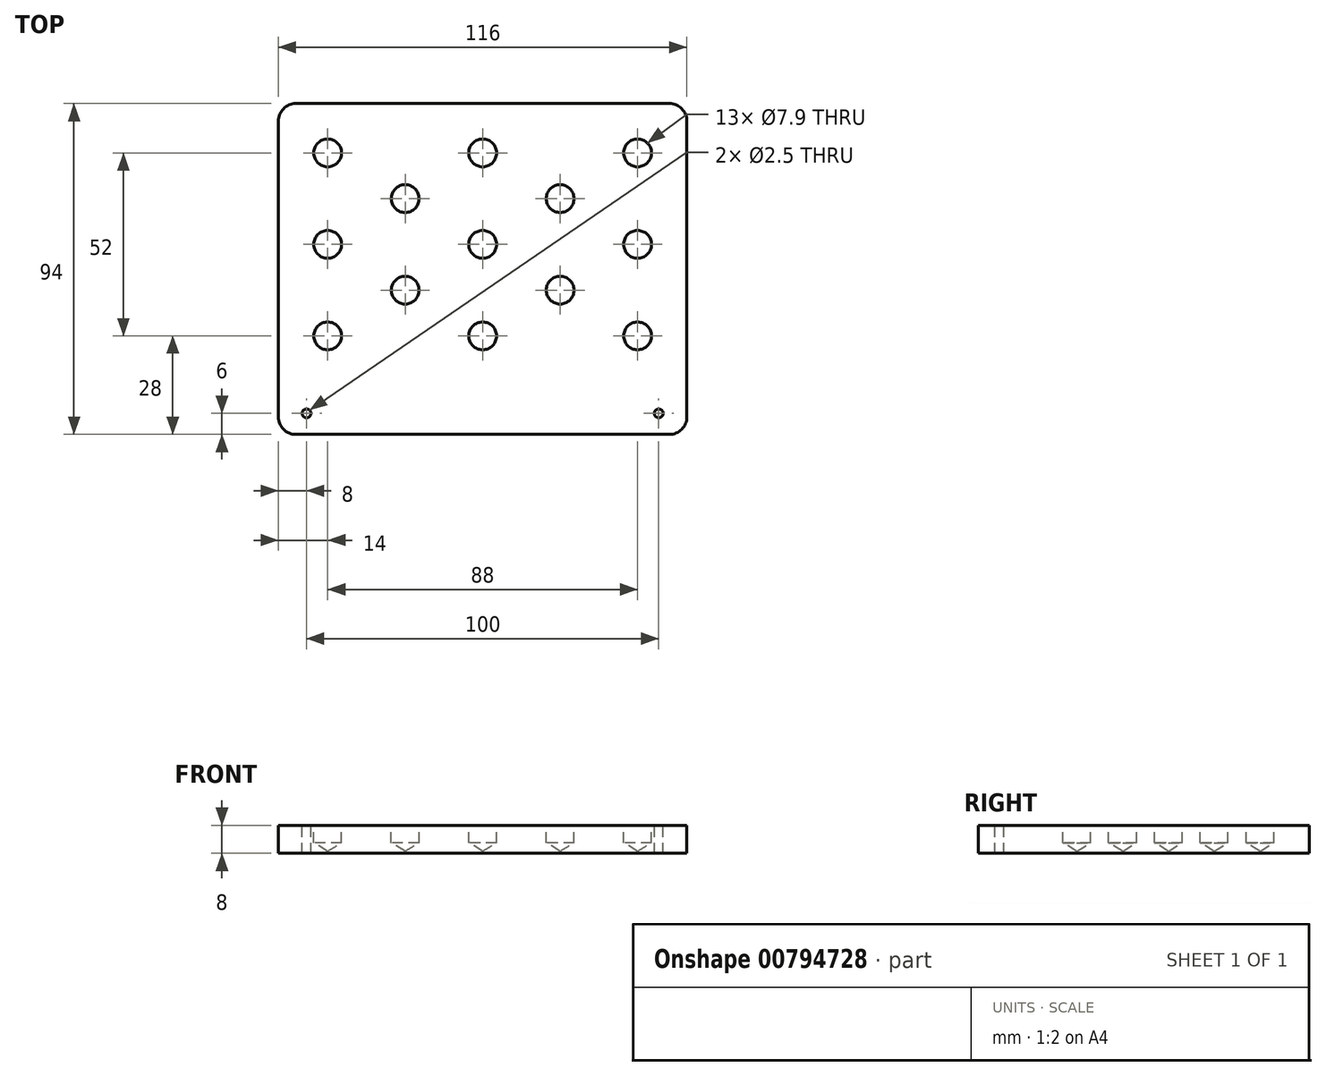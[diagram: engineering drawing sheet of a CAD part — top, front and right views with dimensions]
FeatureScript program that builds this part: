
annotation { "Feature Type Name" : "Feature", "Feature Type Description" : "" }
export const myFeature = defineFeature(function(context is Context, id is Id, definition is map)
    precondition{}
    {
        {
            var Q0;
            Q0=qCreatedBy(makeId("Top.planeOp"),FACE);
            var sketch = newSketch(context, id + "F0", { "sketchPlane" : qUnion([Q0])});
            skLineSegment(sketch, "E0.bottom", {"start": v(-58, 47) * mm, "end": v(58, 47) * mm});
            skLineSegment(sketch, "E0.top", {"start": v(-58, -47) * mm, "end": v(58, -47) * mm});
            skLineSegment(sketch, "E0.left", {"start": v(-58, 47) * mm, "end": v(-58, -47) * mm});
            skLineSegment(sketch, "E0.right", {"start": v(58, 47) * mm, "end": v(58, -47) * mm});
            skPoint(sketch, "E0.middle", {"position": v(0, 0) * mm});
            skSolve(sketch);
        }
        {
            var Q0;
            Q0=makeQuery(id+"F0.imprint","IMPRINT",FACE,{"disambiguationData":[TD([[makeQuery(id+"F0.imprint","IMPRINT",EDGE,{"derivedFrom":sQuery(id+"F0.wireOp",EDGE,"E0.bottom")}),-1.0]])]});
            extrude(context, id + "F1", {"entities" : qUnion([Q0]), "depth" : 8 * mm, "offsetDistance" : 25 * mm});
        }
        {
            var Q0;
            Q0=makeQuery(id+"F1.opExtrude","CAP_FACE",FACE,{"disambiguationData":[OSD([sQuery(id+"F0.wireOp",EDGE,"E0.bottom"),sQuery(id+"F0.wireOp",EDGE,"E0.top"),sQuery(id+"F0.wireOp",EDGE,"E0.left"),sQuery(id+"F0.wireOp",EDGE,"E0.right")])],"isStart":false});
            var sketch = newSketch(context, id + "F2", { "sketchPlane" : qUnion([Q0])});
            skLineSegment(sketch, "E1", {"start": v(-58, -32) * mm, "end": v(58, -32) * mm, "construction": true});
            skLineSegment(sketch, "E2", {"start": v(-58, -19) * mm, "end": v(58, -19) * mm, "construction": true});
            skLineSegment(sketch, "E3", {"start": v(58, -19) * mm, "end": v(58, -6) * mm, "construction": true});
            skLineSegment(sketch, "E4", {"start": v(58, -6) * mm, "end": v(-58, -6) * mm, "construction": true});
            skLineSegment(sketch, "E5", {"start": v(-58, -6) * mm, "end": v(-58, 7) * mm, "construction": true});
            skLineSegment(sketch, "E6", {"start": v(-58, 7) * mm, "end": v(58, 7) * mm, "construction": true});
            skLineSegment(sketch, "E7", {"start": v(58, 7) * mm, "end": v(58, 20) * mm, "construction": true});
            skLineSegment(sketch, "E8", {"start": v(58, 20) * mm, "end": v(-58, 20) * mm, "construction": true});
            skLineSegment(sketch, "E9.bottom", {"start": v(-58, -37) * mm, "end": v(58, -37) * mm, "construction": true});
            skLineSegment(sketch, "E9.top", {"start": v(-58, -45) * mm, "end": v(58, -45) * mm, "construction": true});
            skLineSegment(sketch, "E9.left", {"start": v(-58, -37) * mm, "end": v(-58, -45) * mm, "construction": true});
            skLineSegment(sketch, "E9.right", {"start": v(58, -37) * mm, "end": v(58, -45) * mm, "construction": true});
            skLineSegment(sketch, "E10", {"start": v(-44, 47) * mm, "end": v(-44, -32) * mm, "construction": true});
            skLineSegment(sketch, "E11", {"start": v(-44, -32) * mm, "end": v(-22, -32) * mm, "construction": true});
            skLineSegment(sketch, "E12", {"start": v(-22, -32) * mm, "end": v(-22, 47) * mm, "construction": true});
            skLineSegment(sketch, "E13", {"start": v(-22, 47) * mm, "end": v(0, 47) * mm, "construction": true});
            skLineSegment(sketch, "E14", {"start": v(0, 47) * mm, "end": v(0, -32) * mm, "construction": true});
            skLineSegment(sketch, "E15", {"start": v(0, -32) * mm, "end": v(22, -32) * mm, "construction": true});
            skLineSegment(sketch, "E16", {"start": v(22, -32) * mm, "end": v(22, 47) * mm, "construction": true});
            skLineSegment(sketch, "E17", {"start": v(22, 47) * mm, "end": v(44, 47) * mm, "construction": true});
            skLineSegment(sketch, "E18", {"start": v(44, 47) * mm, "end": v(44, -32) * mm, "construction": true});
            skLineSegment(sketch, "E19", {"start": v(44, -32) * mm, "end": v(44.94, -32) * mm, "construction": true});
            skPoint(sketch, "E20", {"position": v(-44, 7) * mm});
            skPoint(sketch, "E21", {"position": v(-44, -6) * mm});
            skPoint(sketch, "E22", {"position": v(-22, -19) * mm});
            skPoint(sketch, "E23", {"position": v(-22, 20) * mm});
            skPoint(sketch, "E24", {"position": v(0, 7) * mm});
            skPoint(sketch, "E25", {"position": v(0, -6) * mm});
            skPoint(sketch, "E26", {"position": v(22, -19) * mm});
            skPoint(sketch, "E27", {"position": v(22, 7) * mm});
            skCircle(sketch, "E28", {"center": v(-44, 7) * mm, "radius": 12 * mm});
            skCircle(sketch, "E29", {"center": v(-22, 20) * mm, "radius": 12 * mm});
            skPoint(sketch, "E30", {"position": v(-22, -6) * mm});
            skCircle(sketch, "E31", {"center": v(-22, -6) * mm, "radius": 12 * mm});
            skCircle(sketch, "E32", {"center": v(0, 7) * mm, "radius": 12 * mm});
            skPoint(sketch, "E33", {"position": v(-44, -19) * mm});
            skPoint(sketch, "E34", {"position": v(0, -19) * mm});
            skPoint(sketch, "E35", {"position": v(22, 20) * mm});
            skPoint(sketch, "E36", {"position": v(22, -6) * mm});
            skCircle(sketch, "E37", {"center": v(-44, -19) * mm, "radius": 12 * mm});
            skCircle(sketch, "E38", {"center": v(0, -19) * mm, "radius": 12 * mm});
            skCircle(sketch, "E39", {"center": v(22, -6) * mm, "radius": 12 * mm});
            skCircle(sketch, "E40", {"center": v(22, 20) * mm, "radius": 12 * mm});
            skPoint(sketch, "E41", {"position": v(44, 7) * mm});
            skPoint(sketch, "E42", {"position": v(44, -19) * mm});
            skCircle(sketch, "E43", {"center": v(44, 7) * mm, "radius": 12 * mm});
            skCircle(sketch, "E44", {"center": v(44, -19) * mm, "radius": 12 * mm});
            skLineSegment(sketch, "E45", {"start": v(-58, 33) * mm, "end": v(58, 33) * mm, "construction": true});
            skPoint(sketch, "E46", {"position": v(-44, 33) * mm});
            skPoint(sketch, "E47", {"position": v(0, 33) * mm});
            skPoint(sketch, "E48", {"position": v(44, 33) * mm});
            skCircle(sketch, "E49", {"center": v(-44, 33) * mm, "radius": 12 * mm});
            skCircle(sketch, "E50", {"center": v(0, 33) * mm, "radius": 12 * mm});
            skCircle(sketch, "E51", {"center": v(44, 33) * mm, "radius": 12 * mm});
            skSolve(sketch);
        }
        {
            var Q0;
            Q0=sQuery(id+"F2.wireOp",VERTEX,"E46");
            var Q1;
            Q1=sQuery(id+"F2.wireOp",VERTEX,"E23");
            var Q2;
            Q2=sQuery(id+"F2.wireOp",VERTEX,"E20");
            var Q3;
            Q3=sQuery(id+"F2.wireOp",VERTEX,"E33");
            var Q4;
            Q4=sQuery(id+"F2.wireOp",VERTEX,"E30");
            var Q5;
            Q5=sQuery(id+"F2.wireOp",VERTEX,"E34");
            var Q6;
            Q6=sQuery(id+"F2.wireOp",VERTEX,"E24");
            var Q7;
            Q7=sQuery(id+"F2.wireOp",VERTEX,"E47");
            var Q8;
            Q8=sQuery(id+"F2.wireOp",VERTEX,"E35");
            var Q9;
            Q9=sQuery(id+"F2.wireOp",VERTEX,"E36");
            var Q10;
            Q10=sQuery(id+"F2.wireOp",VERTEX,"E41");
            var Q11;
            Q11=sQuery(id+"F2.wireOp",VERTEX,"E48");
            var Q12;
            Q12=sQuery(id+"F2.wireOp",VERTEX,"E42");
            var Q13;
            Q13=makeQuery(id+"F1.opExtrude","SWEPT_BODY",BODY,{"disambiguationData":[OSD([sQuery(id+"F0.wireOp",EDGE,"E0.bottom"),sQuery(id+"F0.wireOp",EDGE,"E0.top"),sQuery(id+"F0.wireOp",EDGE,"E0.left"),sQuery(id+"F0.wireOp",EDGE,"E0.right")])]});
            hole(context, id + "F3", {"style" : HoleStyle.SIMPLE, "endStyle" : HoleEndStyle.BLIND, "standardTappedOrClearance" : lookupTablePath({ "standard" : "ISO", "size" : "7.9", "type" : "Drilled" }), "standardBlindInLast" : lookupTablePath({ "standard" : "ISO", "size" : "7.9", "type" : "Drilled" }), "holeDiameter" : 7.9 * mm, "majorDiameter" : 5 * mm, "holeDepth" : 5 * mm, "isTappedThrough" : true, "tappedDepth" : 12 * mm, "tapClearance" : 3, "locations" : qUnion([Q0, Q1, Q2, Q3, Q4, Q5, Q6, Q7, Q8, Q9, Q10, Q11, Q12]), "scope" : qUnion([Q13])});
        }
        {
            var Q0;
            Q0=makeQuery(id+"F1.opExtrude","CAP_FACE",FACE,{"disambiguationData":[OSD([sQuery(id+"F0.wireOp",EDGE,"E0.bottom"),sQuery(id+"F0.wireOp",EDGE,"E0.top"),sQuery(id+"F0.wireOp",EDGE,"E0.left"),sQuery(id+"F0.wireOp",EDGE,"E0.right")])],"isStart":false});
            var sketch = newSketch(context, id + "F4", { "sketchPlane" : qUnion([Q0])});
            skLineSegment(sketch, "E52", {"start": v(-58, -41) * mm, "end": v(58, -41) * mm, "construction": true});
            skPoint(sketch, "E53", {"position": v(-50, -41) * mm});
            skPoint(sketch, "E54", {"position": v(50, -41) * mm});
            skSolve(sketch);
        }
        {
            var Q0;
            Q0=sQuery(id+"F4.wireOp",VERTEX,"E53");
            var Q1;
            Q1=sQuery(id+"F4.wireOp",VERTEX,"E54");
            var Q2;
            Q2=makeQuery(id+"F1.opExtrude","SWEPT_BODY",BODY,{"disambiguationData":[OSD([sQuery(id+"F0.wireOp",EDGE,"E0.bottom"),sQuery(id+"F0.wireOp",EDGE,"E0.top"),sQuery(id+"F0.wireOp",EDGE,"E0.left"),sQuery(id+"F0.wireOp",EDGE,"E0.right")])]});
            hole(context, id + "F5", {"style" : HoleStyle.SIMPLE, "endStyle" : HoleEndStyle.THROUGH, "standardTappedOrClearance" : lookupTablePath({ "standard" : "ISO", "engagement" : "75%", "pitch" : "0.5 mm", "size" : "M3", "type" : "Tapped" }), "standardBlindInLast" : lookupTablePath({ "standard" : "ISO", "engagement" : "75%", "pitch" : "0.5 mm", "size" : "M3", "type" : "Tapped" }), "holeDiameter" : 2.5 * mm, "majorDiameter" : 3 * mm, "showTappedDepth" : true, "isTappedThrough" : true, "tappedDepth" : 12 * mm, "tapClearance" : 3, "locations" : qUnion([Q0, Q1]), "scope" : qUnion([Q2])});
        }
        {
            var Q0;
            Q0=makeQuery(id+"F1.opExtrude","SWEPT_EDGE",EDGE,{"disambiguationData":[OSD([sQuery(id+"F0.wireOp",EDGE,"E0.top"),sQuery(id+"F0.wireOp",EDGE,"E0.left")])]});
            var Q1;
            Q1=makeQuery(id+"F1.opExtrude","SWEPT_EDGE",EDGE,{"disambiguationData":[OSD([sQuery(id+"F0.wireOp",EDGE,"E0.top"),sQuery(id+"F0.wireOp",EDGE,"E0.right")])]});
            var Q2;
            Q2=makeQuery(id+"F1.opExtrude","SWEPT_EDGE",EDGE,{"disambiguationData":[OSD([sQuery(id+"F0.wireOp",EDGE,"E0.bottom"),sQuery(id+"F0.wireOp",EDGE,"E0.left")])]});
            var Q3;
            Q3=makeQuery(id+"F1.opExtrude","SWEPT_EDGE",EDGE,{"disambiguationData":[OSD([sQuery(id+"F0.wireOp",EDGE,"E0.bottom"),sQuery(id+"F0.wireOp",EDGE,"E0.right")])]});
            fillet(context, id + "F6", {"entities" : qUnion([Q0, Q1, Q2, Q3]), "radius" : 5 * mm, "tangentPropagation" : true, "allowEdgeOverflow" : false});
        }
    });
